FCSTD DOCUMENT  (FreeCAD 1.0R39285 (Git))
Label: folding_chair_02
License: CERN Open Hardware Licence permissive
LicenseURL: https://cern-ohl.web.cern.ch/
objects: Part::Feature×9, Sketcher::SketchObject×3, PartDesign::Body×2, Image::ImagePlane×1, PartDesign::SubShapeBinder×1
note: 18 computed .brp shape members not serialized (recipe doc carries the construction recipe); baked Part::Feature solids carry a one-line shape summary decoded from their .brp

FEATURE [Image::ImagePlane] flat_folding_chair_04
  Placement = pos=(40,-70,0) rot=(0,0,1;0rad)
  XSize = 80.0169
  YSize = 119.179
FEATURE [Part::Feature] path4
  shape: bbox 82.94 x 138.4 x 2e-07 mm, 0 faces, 0 solids (baked)
FEATURE [Part::Feature] path005
  shape: bbox 70.38 x 121.7 x 2e-07 mm, 0 faces, 0 solids (baked)
FEATURE [Part::Feature] path006
  shape: bbox 67.79 x 116.9 x 2e-07 mm, 0 faces, 0 solids (baked)
FEATURE [Part::Feature] path007
  shape: bbox 15.73 x 19.43 x 2e-07 mm, 0 faces, 0 solids (baked)
FEATURE [Part::Feature] path008
  shape: bbox 52.24 x 59.71 x 2e-07 mm, 0 faces, 0 solids (baked)
FEATURE [Part::Feature] path009
  shape: bbox 2.06 x 3.665 x 2e-07 mm, 0 faces, 0 solids (baked)
FEATURE [Part::Feature] path010
  shape: bbox 1.824 x 3.568 x 2e-07 mm, 0 faces, 0 solids (baked)
FEATURE [Part::Feature] path011
  shape: bbox 4.443 x 14.85 x 2e-07 mm, 0 faces, 0 solids (baked)
FEATURE [Part::Feature] path012
  shape: bbox 4.616 x 15.29 x 2e-07 mm, 0 faces, 0 solids (baked)
FEATURE [Sketcher::SketchObject] Sketch
  ArcFitTolerance = 1e-06
  AttachmentSupport = -> [XY_Plane]
  FullyConstrained = true
  MakeInternals = false
  MapMode = 5
  sketch-geometry (37):
    g0: LineSegment StartX=0 StartY=0 StartZ=0 EndX=0 EndY=-138.5 EndZ=0
    g1: LineSegment StartX=0 StartY=-138.5 StartZ=0 EndX=83 EndY=-138.5 EndZ=0
    g2: LineSegment StartX=83 StartY=-138.5 StartZ=0 EndX=83 EndY=0 EndZ=0
    g3: LineSegment StartX=83 StartY=0 StartZ=0 EndX=0 EndY=0 EndZ=0
    g4: LineSegment StartX=21.5 StartY=-68.75 StartZ=0 EndX=21.5 EndY=-128.75 EndZ=0
    g5: LineSegment StartX=21.5 StartY=-128.75 StartZ=0 EndX=61.5 EndY=-128.75 EndZ=0
    g6: LineSegment StartX=61.5 StartY=-128.75 StartZ=0 EndX=61.5 EndY=-68.75 EndZ=0
    g7: LineSegment StartX=61.5 StartY=-68.75 StartZ=0 EndX=21.5 EndY=-68.75 EndZ=0
    g8: LineSegment StartX=32.75 StartY=-63.75 StartZ=0 EndX=32.75 EndY=-68.75 EndZ=0
    g9: LineSegment StartX=32.75 StartY=-68.75 StartZ=0 EndX=50.25 EndY=-68.75 EndZ=0
    g10: LineSegment StartX=50.25 StartY=-68.75 StartZ=0 EndX=50.25 EndY=-63.75 EndZ=0
    g11: LineSegment StartX=50.25 StartY=-63.75 StartZ=0 EndX=32.75 EndY=-63.75 EndZ=0
    g12: LineSegment StartX=15.5 StartY=-10.75 StartZ=0 EndX=15.5 EndY=-48.75 EndZ=0
    g13: LineSegment StartX=15.5 StartY=-48.75 StartZ=0 EndX=67.5 EndY=-48.75 EndZ=0
    g14: LineSegment StartX=67.5 StartY=-48.75 StartZ=0 EndX=67.5 EndY=-10.75 EndZ=0
    g15: LineSegment StartX=67.5 StartY=-10.75 StartZ=0 EndX=15.5 EndY=-10.75 EndZ=0
    g16: LineSegment StartX=7.8 StartY=-10.75 StartZ=0 EndX=7.8 EndY=-50.25 EndZ=0
    g17: LineSegment StartX=7.8 StartY=-50.25 StartZ=0 EndX=14 EndY=-50.25 EndZ=0
    g18: LineSegment StartX=14 StartY=-50.25 StartZ=0 EndX=14 EndY=-10.75 EndZ=0
    g19: LineSegment StartX=14 StartY=-10.75 StartZ=0 EndX=7.8 EndY=-10.75 EndZ=0
    g20: LineSegment StartX=69 StartY=-10.75 StartZ=0 EndX=69 EndY=-50.25 EndZ=0
    g21: LineSegment StartX=69 StartY=-50.25 StartZ=0 EndX=75.2 EndY=-50.25 EndZ=0
    g22: LineSegment StartX=75.2 StartY=-50.25 StartZ=0 EndX=75.2 EndY=-10.75 EndZ=0
    g23: LineSegment StartX=75.2 StartY=-10.75 StartZ=0 EndX=69 EndY=-10.75 EndZ=0
    g24: LineSegment StartX=14 StartY=-135.25 StartZ=0 EndX=14 EndY=-138.5 EndZ=0
    g25: LineSegment StartX=14 StartY=-138.5 StartZ=0 EndX=69 EndY=-138.5 EndZ=0
    g26: LineSegment StartX=69 StartY=-138.5 StartZ=0 EndX=69 EndY=-135.25 EndZ=0
    g27: LineSegment StartX=69 StartY=-135.25 StartZ=0 EndX=14 EndY=-135.25 EndZ=0
    g28: LineSegment [constr] StartX=41.5 StartY=-138.5 StartZ=0 EndX=41.5 EndY=-135.25 EndZ=0
    g29: LineSegment [constr] StartX=41.5 StartY=-135.25 StartZ=0 EndX=41.5 EndY=-128.75 EndZ=0
    g30: LineSegment [constr] StartX=41.5 StartY=-128.75 StartZ=0 EndX=41.5 EndY=-94.75 EndZ=0
    g31: LineSegment [constr] StartX=41.5 StartY=-94.75 StartZ=0 EndX=41.5 EndY=-68.75 EndZ=0
    g32: LineSegment [constr] StartX=41.5 StartY=-68.75 StartZ=0 EndX=41.5 EndY=-63.75 EndZ=0
    g33: LineSegment [constr] StartX=41.5 StartY=-63.75 StartZ=0 EndX=41.5 EndY=-48.75 EndZ=0
    g34: LineSegment [constr] StartX=41.5 StartY=-48.75 StartZ=0 EndX=41.5 EndY=-10.75 EndZ=0
    g35: LineSegment [constr] StartX=41.5 StartY=-10.75 StartZ=0 EndX=41.5 EndY=0 EndZ=0
    g36: Circle [constr] CenterX=15.5 CenterY=-48.75 CenterZ=0 NormalX=0 NormalY=0 NormalZ=1 AngleXU=0 Radius=1.5
  constraints (102):
    c: Coincident(g0,g1)
    c: Coincident(g1,g2)
    c: Coincident(g2,g3)
    c: Coincident(g3,g0)
    c: Vertical(g0)
    c: Vertical(g2)
    c: Horizontal(g1)
    c: Horizontal(g3)
    c: Coincident(g0,g-1)
    c: DistanceX(g3,g3) = 83
    c: DistanceY(g0,g0) = 138.5
    c: Coincident(g4,g5)
    c: Coincident(g5,g6)
    c: Coincident(g6,g7)
    c: Coincident(g7,g4)
    c: Vertical(g4)
    c: Vertical(g6)
    c: Horizontal(g5)
    c: Horizontal(g7)
    c: Coincident(g8,g9)
    c: Coincident(g9,g10)
    c: Coincident(g10,g11)
    c: Coincident(g11,g8)
    c: Vertical(g8)
    c: Vertical(g10)
    c: Horizontal(g9)
    c: Horizontal(g11)
    c: Coincident(g12,g13)
    c: Coincident(g13,g14)
    c: Coincident(g14,g15)
    c: Coincident(g15,g12)
    c: Vertical(g12)
    c: Vertical(g14)
    c: Horizontal(g13)
    c: Horizontal(g15)
    c: Coincident(g16,g17)
    c: Coincident(g17,g18)
    c: Coincident(g18,g19)
    c: Coincident(g19,g16)
    c: Vertical(g16)
    c: Vertical(g18)
    c: Horizontal(g17)
    c: Horizontal(g19)
    c: Coincident(g20,g21)
    c: Coincident(g21,g22)
    c: Coincident(g22,g23)
    c: Coincident(g23,g20)
    c: Vertical(g20)
    c: Vertical(g22)
    c: Horizontal(g21)
    c: Horizontal(g23)
    c: Coincident(g24,g25)
    c: Coincident(g25,g26)
    c: Coincident(g26,g27)
    c: Coincident(g27,g24)
    c: Vertical(g24)
    c: Vertical(g26)
    c: Horizontal(g25)
    c: Horizontal(g27)
    c: Symmetric(g1,g1,g28)
    c: Coincident(g29,g28)
    c: Coincident(g30,g29)
    c: Vertical(g30)
    c: Coincident(g31,g30)
    c: Symmetric(g7,g7,g31)
    c: Coincident(g32,g31)
    c: Symmetric(g11,g11,g32)
    c: Coincident(g33,g32)
    c: Symmetric(g13,g13,g33)
    c: Vertical(g33)
    c: Coincident(g34,g33)
    c: Symmetric(g15,g15,g34)
    c: Coincident(g35,g34)
    c: Symmetric(g3,g3,g35)
    c: Vertical(g35)
    c: Vertical(g28)
    c: Vertical(g29)
    c: PointOnObject(g28,g27)
    c: PointOnObject(g29,g5)
    c: Vertical(g32)
    c: Symmetric(g24,g25,g28)
    c: Distance(g24,g24) = 3.25
    c: DistanceX(g27,g27) = 55
    c: DistanceY(g29,g29) = 6.5
    c: DistanceX(g5,g5) = 40
    c: DistanceY(g4,g4) = 60
    c: PointOnObject(g31,g9)
    c: DistanceY(g8,g8) = 5
    c: DistanceX(g11,g11) = 17.5
    c: DistanceY(g33,g33) = 15
    c: DistanceX(g13,g13) = 52
    c: DistanceY(g12,g12) = 38
    c: Equal(g19,g23)
    c: Equal(g18,g20)
    c: Symmetric(g18,g20,g35)
    c: Horizontal(g18,g12)
    c: DistanceX(g19,g19) = 6.2
    c: Distance(g18,g12) = 1.5
    c: DistanceY(g30,g30) = 34
    c: Coincident(g36,g12)
    c: Tangent(g36,g18)
    c: Tangent(g17,g36)
FEATURE [PartDesign::Body] Body
  AllowCompound = false
  Group = -> [Sketch]
  Origin = -> Origin
FEATURE [Sketcher::SketchObject] Sketch001
  ArcFitTolerance = 1e-06
  FullyConstrained = false
  MakeInternals = false
  sketch-geometry (161):
    g0: BSplineCurve PolesCount=2 KnotsCount=2 Degree=1 IsPeriodic=0
    g1: BSplineCurve PolesCount=2 KnotsCount=2 Degree=1 IsPeriodic=0
    g2: BSplineCurve PolesCount=2 KnotsCount=2 Degree=1 IsPeriodic=0
    g3: BSplineCurve PolesCount=2 KnotsCount=2 Degree=1 IsPeriodic=0
    g4: BSplineCurve PolesCount=2 KnotsCount=2 Degree=1 IsPeriodic=0
    g5: BSplineCurve PolesCount=2 KnotsCount=2 Degree=1 IsPeriodic=0
    g6: BSplineCurve PolesCount=4 KnotsCount=2 Degree=3 IsPeriodic=0
    g7: BSplineCurve PolesCount=4 KnotsCount=2 Degree=3 IsPeriodic=0
    g8: BSplineCurve PolesCount=2 KnotsCount=2 Degree=1 IsPeriodic=0
    g9: BSplineCurve PolesCount=2 KnotsCount=2 Degree=1 IsPeriodic=0
    g10: BSplineCurve PolesCount=2 KnotsCount=2 Degree=1 IsPeriodic=0
    g11: BSplineCurve PolesCount=2 KnotsCount=2 Degree=1 IsPeriodic=0
    g12: BSplineCurve PolesCount=4 KnotsCount=2 Degree=3 IsPeriodic=0
    g13: BSplineCurve PolesCount=4 KnotsCount=2 Degree=3 IsPeriodic=0
    g14: BSplineCurve PolesCount=4 KnotsCount=2 Degree=3 IsPeriodic=0
    g15: BSplineCurve PolesCount=4 KnotsCount=2 Degree=3 IsPeriodic=0
    g16: BSplineCurve PolesCount=4 KnotsCount=2 Degree=3 IsPeriodic=0
    g17: BSplineCurve PolesCount=4 KnotsCount=2 Degree=3 IsPeriodic=0
    g18: BSplineCurve PolesCount=4 KnotsCount=2 Degree=3 IsPeriodic=0
    g19: BSplineCurve PolesCount=4 KnotsCount=2 Degree=3 IsPeriodic=0
    g20: BSplineCurve PolesCount=4 KnotsCount=2 Degree=3 IsPeriodic=0
    g21: BSplineCurve PolesCount=4 KnotsCount=2 Degree=3 IsPeriodic=0
    g22: BSplineCurve PolesCount=4 KnotsCount=2 Degree=3 IsPeriodic=0
    g23: BSplineCurve PolesCount=4 KnotsCount=2 Degree=3 IsPeriodic=0
    g24: BSplineCurve PolesCount=4 KnotsCount=2 Degree=3 IsPeriodic=0
    g25: BSplineCurve PolesCount=4 KnotsCount=2 Degree=3 IsPeriodic=0
    g26: BSplineCurve PolesCount=2 KnotsCount=2 Degree=1 IsPeriodic=0
    g27: BSplineCurve PolesCount=2 KnotsCount=2 Degree=1 IsPeriodic=0
    g28: BSplineCurve PolesCount=4 KnotsCount=2 Degree=3 IsPeriodic=0
    g29: BSplineCurve PolesCount=4 KnotsCount=2 Degree=3 IsPeriodic=0
    g30: BSplineCurve PolesCount=2 KnotsCount=2 Degree=1 IsPeriodic=0
    g31: BSplineCurve PolesCount=2 KnotsCount=2 Degree=1 IsPeriodic=0
    g32: BSplineCurve PolesCount=4 KnotsCount=2 Degree=3 IsPeriodic=0
    g33: BSplineCurve PolesCount=4 KnotsCount=2 Degree=3 IsPeriodic=0
    g34: BSplineCurve PolesCount=2 KnotsCount=2 Degree=1 IsPeriodic=0
    g35: BSplineCurve PolesCount=2 KnotsCount=2 Degree=1 IsPeriodic=0
    g36: BSplineCurve PolesCount=2 KnotsCount=2 Degree=1 IsPeriodic=0
    g37: BSplineCurve PolesCount=2 KnotsCount=2 Degree=1 IsPeriodic=0
    g38: BSplineCurve PolesCount=4 KnotsCount=2 Degree=3 IsPeriodic=0
    g39: BSplineCurve PolesCount=4 KnotsCount=2 Degree=3 IsPeriodic=0
    g40: BSplineCurve PolesCount=4 KnotsCount=2 Degree=3 IsPeriodic=0
    g41: BSplineCurve PolesCount=4 KnotsCount=2 Degree=3 IsPeriodic=0
    g42: BSplineCurve PolesCount=4 KnotsCount=2 Degree=3 IsPeriodic=0
    g43: BSplineCurve PolesCount=4 KnotsCount=2 Degree=3 IsPeriodic=0
    g44: BSplineCurve PolesCount=4 KnotsCount=2 Degree=3 IsPeriodic=0
    g45: BSplineCurve PolesCount=4 KnotsCount=2 Degree=3 IsPeriodic=0
    g46: BSplineCurve PolesCount=4 KnotsCount=2 Degree=3 IsPeriodic=0
    g47: BSplineCurve PolesCount=2 KnotsCount=2 Degree=1 IsPeriodic=0
    g48: BSplineCurve PolesCount=2 KnotsCount=2 Degree=1 IsPeriodic=0
    g49: BSplineCurve PolesCount=4 KnotsCount=2 Degree=3 IsPeriodic=0
    g50: BSplineCurve PolesCount=4 KnotsCount=2 Degree=3 IsPeriodic=0
    g51: BSplineCurve PolesCount=2 KnotsCount=2 Degree=1 IsPeriodic=0
    g52: BSplineCurve PolesCount=2 KnotsCount=2 Degree=1 IsPeriodic=0
    g53: BSplineCurve PolesCount=4 KnotsCount=2 Degree=3 IsPeriodic=0
    g54: BSplineCurve PolesCount=4 KnotsCount=2 Degree=3 IsPeriodic=0
    g55: BSplineCurve PolesCount=4 KnotsCount=2 Degree=3 IsPeriodic=0
    g56: BSplineCurve PolesCount=2 KnotsCount=2 Degree=1 IsPeriodic=0
    g57: BSplineCurve PolesCount=2 KnotsCount=2 Degree=1 IsPeriodic=0
    g58: BSplineCurve PolesCount=4 KnotsCount=2 Degree=3 IsPeriodic=0
    g59: BSplineCurve PolesCount=4 KnotsCount=2 Degree=3 IsPeriodic=0
    g60: BSplineCurve PolesCount=4 KnotsCount=2 Degree=3 IsPeriodic=0
    g61: BSplineCurve PolesCount=2 KnotsCount=2 Degree=1 IsPeriodic=0
    g62: BSplineCurve PolesCount=2 KnotsCount=2 Degree=1 IsPeriodic=0
    g63: BSplineCurve PolesCount=2 KnotsCount=2 Degree=1 IsPeriodic=0
    g64: BSplineCurve PolesCount=2 KnotsCount=2 Degree=1 IsPeriodic=0
    g65: BSplineCurve PolesCount=2 KnotsCount=2 Degree=1 IsPeriodic=0
    g66: BSplineCurve PolesCount=4 KnotsCount=2 Degree=3 IsPeriodic=0
    g67: BSplineCurve PolesCount=4 KnotsCount=2 Degree=3 IsPeriodic=0
    g68: BSplineCurve PolesCount=4 KnotsCount=2 Degree=3 IsPeriodic=0
    g69: BSplineCurve PolesCount=2 KnotsCount=2 Degree=1 IsPeriodic=0
    g70: BSplineCurve PolesCount=2 KnotsCount=2 Degree=1 IsPeriodic=0
    g71: BSplineCurve PolesCount=4 KnotsCount=2 Degree=3 IsPeriodic=0
    g72: BSplineCurve PolesCount=4 KnotsCount=2 Degree=3 IsPeriodic=0
    g73: BSplineCurve PolesCount=4 KnotsCount=2 Degree=3 IsPeriodic=0
    g74: BSplineCurve PolesCount=4 KnotsCount=2 Degree=3 IsPeriodic=0
    g75: BSplineCurve PolesCount=2 KnotsCount=2 Degree=1 IsPeriodic=0
    g76: BSplineCurve PolesCount=2 KnotsCount=2 Degree=1 IsPeriodic=0
    g77: BSplineCurve PolesCount=2 KnotsCount=2 Degree=1 IsPeriodic=0
    g78: BSplineCurve PolesCount=2 KnotsCount=2 Degree=1 IsPeriodic=0
    g79: BSplineCurve PolesCount=4 KnotsCount=2 Degree=3 IsPeriodic=0
    g80: BSplineCurve PolesCount=4 KnotsCount=2 Degree=3 IsPeriodic=0
    g81: BSplineCurve PolesCount=4 KnotsCount=2 Degree=3 IsPeriodic=0
    g82: BSplineCurve PolesCount=2 KnotsCount=2 Degree=1 IsPeriodic=0
    g83: BSplineCurve PolesCount=2 KnotsCount=2 Degree=1 IsPeriodic=0
    g84: BSplineCurve PolesCount=4 KnotsCount=2 Degree=3 IsPeriodic=0
    g85: BSplineCurve PolesCount=4 KnotsCount=2 Degree=3 IsPeriodic=0
    g86: BSplineCurve PolesCount=2 KnotsCount=2 Degree=1 IsPeriodic=0
    g87: BSplineCurve PolesCount=2 KnotsCount=2 Degree=1 IsPeriodic=0
    g88: BSplineCurve PolesCount=4 KnotsCount=2 Degree=3 IsPeriodic=0
    g89: BSplineCurve PolesCount=4 KnotsCount=2 Degree=3 IsPeriodic=0
    g90: BSplineCurve PolesCount=2 KnotsCount=2 Degree=1 IsPeriodic=0
    g91: BSplineCurve PolesCount=2 KnotsCount=2 Degree=1 IsPeriodic=0
    g92: BSplineCurve PolesCount=4 KnotsCount=2 Degree=3 IsPeriodic=0
    g93: BSplineCurve PolesCount=4 KnotsCount=2 Degree=3 IsPeriodic=0
    g94: BSplineCurve PolesCount=4 KnotsCount=2 Degree=3 IsPeriodic=0
    g95: BSplineCurve PolesCount=4 KnotsCount=2 Degree=3 IsPeriodic=0
    g96: BSplineCurve PolesCount=4 KnotsCount=2 Degree=3 IsPeriodic=0
    g97: BSplineCurve PolesCount=2 KnotsCount=2 Degree=1 IsPeriodic=0
    g98: BSplineCurve PolesCount=2 KnotsCount=2 Degree=1 IsPeriodic=0
    g99: BSplineCurve PolesCount=4 KnotsCount=2 Degree=3 IsPeriodic=0
    g100: BSplineCurve PolesCount=4 KnotsCount=2 Degree=3 IsPeriodic=0
    g101: BSplineCurve PolesCount=4 KnotsCount=2 Degree=3 IsPeriodic=0
    g102: BSplineCurve PolesCount=4 KnotsCount=2 Degree=3 IsPeriodic=0
    g103: BSplineCurve PolesCount=2 KnotsCount=2 Degree=1 IsPeriodic=0
    g104: BSplineCurve PolesCount=2 KnotsCount=2 Degree=1 IsPeriodic=0
    g105: BSplineCurve PolesCount=4 KnotsCount=2 Degree=3 IsPeriodic=0
    g106: BSplineCurve PolesCount=4 KnotsCount=2 Degree=3 IsPeriodic=0
    g107: BSplineCurve PolesCount=4 KnotsCount=2 Degree=3 IsPeriodic=0
    g108: BSplineCurve PolesCount=4 KnotsCount=2 Degree=3 IsPeriodic=0
    g109: BSplineCurve PolesCount=2 KnotsCount=2 Degree=1 IsPeriodic=0
    g110: BSplineCurve PolesCount=4 KnotsCount=2 Degree=3 IsPeriodic=0
    g111: BSplineCurve PolesCount=2 KnotsCount=2 Degree=1 IsPeriodic=0
    g112: BSplineCurve PolesCount=2 KnotsCount=2 Degree=1 IsPeriodic=0
    g113: BSplineCurve PolesCount=4 KnotsCount=2 Degree=3 IsPeriodic=0
    g114: BSplineCurve PolesCount=4 KnotsCount=2 Degree=3 IsPeriodic=0
    g115: BSplineCurve PolesCount=4 KnotsCount=2 Degree=3 IsPeriodic=0
    g116: BSplineCurve PolesCount=4 KnotsCount=2 Degree=3 IsPeriodic=0
    g117: BSplineCurve PolesCount=4 KnotsCount=2 Degree=3 IsPeriodic=0
    g118: BSplineCurve PolesCount=4 KnotsCount=2 Degree=3 IsPeriodic=0
    g119: BSplineCurve PolesCount=4 KnotsCount=2 Degree=3 IsPeriodic=0
    g120: BSplineCurve PolesCount=4 KnotsCount=2 Degree=3 IsPeriodic=0
    g121: BSplineCurve PolesCount=4 KnotsCount=2 Degree=3 IsPeriodic=0
    g122: BSplineCurve PolesCount=4 KnotsCount=2 Degree=3 IsPeriodic=0
    g123: BSplineCurve PolesCount=2 KnotsCount=2 Degree=1 IsPeriodic=0
    g124: BSplineCurve PolesCount=4 KnotsCount=2 Degree=3 IsPeriodic=0
    g125: BSplineCurve PolesCount=4 KnotsCount=2 Degree=3 IsPeriodic=0
    g126: BSplineCurve PolesCount=4 KnotsCount=2 Degree=3 IsPeriodic=0
    g127: BSplineCurve PolesCount=4 KnotsCount=2 Degree=3 IsPeriodic=0
    g128: BSplineCurve PolesCount=2 KnotsCount=2 Degree=1 IsPeriodic=0
    g129: BSplineCurve PolesCount=2 KnotsCount=2 Degree=1 IsPeriodic=0
    g130: BSplineCurve PolesCount=4 KnotsCount=2 Degree=3 IsPeriodic=0
    g131: BSplineCurve PolesCount=4 KnotsCount=2 Degree=3 IsPeriodic=0
    g132: BSplineCurve PolesCount=4 KnotsCount=2 Degree=3 IsPeriodic=0
    g133: BSplineCurve PolesCount=2 KnotsCount=2 Degree=1 IsPeriodic=0
    g134: BSplineCurve PolesCount=2 KnotsCount=2 Degree=1 IsPeriodic=0
    g135: BSplineCurve PolesCount=4 KnotsCount=2 Degree=3 IsPeriodic=0
    g136: BSplineCurve PolesCount=4 KnotsCount=2 Degree=3 IsPeriodic=0
    g137: BSplineCurve PolesCount=4 KnotsCount=2 Degree=3 IsPeriodic=0
    g138: BSplineCurve PolesCount=4 KnotsCount=2 Degree=3 IsPeriodic=0
    g139: BSplineCurve PolesCount=4 KnotsCount=2 Degree=3 IsPeriodic=0
    g140: BSplineCurve PolesCount=4 KnotsCount=2 Degree=3 IsPeriodic=0
    g141: BSplineCurve PolesCount=4 KnotsCount=2 Degree=3 IsPeriodic=0
    g142: BSplineCurve PolesCount=4 KnotsCount=2 Degree=3 IsPeriodic=0
    g143: BSplineCurve PolesCount=4 KnotsCount=2 Degree=3 IsPeriodic=0
    g144: BSplineCurve PolesCount=4 KnotsCount=2 Degree=3 IsPeriodic=0
    g145: BSplineCurve PolesCount=4 KnotsCount=2 Degree=3 IsPeriodic=0
    g146: BSplineCurve PolesCount=4 KnotsCount=2 Degree=3 IsPeriodic=0
    g147: BSplineCurve PolesCount=4 KnotsCount=2 Degree=3 IsPeriodic=0
    g148: BSplineCurve PolesCount=4 KnotsCount=2 Degree=3 IsPeriodic=0
    g149: BSplineCurve PolesCount=4 KnotsCount=2 Degree=3 IsPeriodic=0
    g150: BSplineCurve PolesCount=4 KnotsCount=2 Degree=3 IsPeriodic=0
    g151: BSplineCurve PolesCount=4 KnotsCount=2 Degree=3 IsPeriodic=0
    g152: BSplineCurve PolesCount=4 KnotsCount=2 Degree=3 IsPeriodic=0
    g153: BSplineCurve PolesCount=4 KnotsCount=2 Degree=3 IsPeriodic=0
    g154: BSplineCurve PolesCount=4 KnotsCount=2 Degree=3 IsPeriodic=0
    g155: BSplineCurve PolesCount=2 KnotsCount=2 Degree=1 IsPeriodic=0
    g156: BSplineCurve PolesCount=4 KnotsCount=2 Degree=3 IsPeriodic=0
    g157: BSplineCurve PolesCount=4 KnotsCount=2 Degree=3 IsPeriodic=0
    g158: BSplineCurve PolesCount=4 KnotsCount=2 Degree=3 IsPeriodic=0
    g159: BSplineCurve PolesCount=4 KnotsCount=2 Degree=3 IsPeriodic=0
    g160: BSplineCurve PolesCount=4 KnotsCount=2 Degree=3 IsPeriodic=0
  constraints (161):
    c: Coincident(g0,g1)
    c: Coincident(g1,g2)
    c: Coincident(g2,g3)
    c: Coincident(g3,g4)
    c: Coincident(g4,g5)
    c: Coincident(g5,g6)
    c: Coincident(g6,g7)
    c: Coincident(g7,g8)
    c: Coincident(g8,g9)
    c: Coincident(g9,g10)
    c: Coincident(g10,g11)
    c: Coincident(g11,g12)
    c: Coincident(g12,g13)
    c: Coincident(g13,g14)
    c: Coincident(g14,g15)
    c: Coincident(g15,g16)
    c: Coincident(g16,g17)
    c: Coincident(g17,g18)
    c: Coincident(g18,g19)
    c: Coincident(g19,g20)
    c: Coincident(g20,g21)
    c: Coincident(g21,g22)
    c: Coincident(g22,g23)
    c: Coincident(g23,g24)
    c: Coincident(g24,g25)
    c: Coincident(g25,g26)
    c: Coincident(g26,g27)
    c: Coincident(g27,g0)
    c: Coincident(g28,g29)
    c: Coincident(g29,g30)
    c: Coincident(g30,g31)
    c: Coincident(g31,g32)
    c: Coincident(g32,g33)
    c: Coincident(g33,g34)
    c: Coincident(g34,g35)
    c: Coincident(g35,g36)
    c: Coincident(g36,g37)
    c: Coincident(g37,g38)
    c: Coincident(g38,g39)
    c: Coincident(g39,g40)
    c: Coincident(g40,g41)
    c: Coincident(g41,g42)
    c: Coincident(g42,g43)
    c: Coincident(g43,g44)
    c: Coincident(g44,g45)
    c: Coincident(g45,g46)
    c: Coincident(g46,g47)
    c: Coincident(g47,g48)
    c: Coincident(g48,g49)
    c: Coincident(g49,g50)
    c: Coincident(g50,g51)
    c: Coincident(g51,g52)
    c: Coincident(g52,g53)
    c: Coincident(g53,g54)
    c: Coincident(g54,g55)
    c: Coincident(g55,g56)
    c: Coincident(g56,g57)
    c: Coincident(g57,g58)
    c: Coincident(g58,g59)
    c: Coincident(g59,g60)
    c: Coincident(g60,g61)
    c: Coincident(g61,g28)
    c: Coincident(g62,g63)
    c: Coincident(g63,g64)
    c: Coincident(g64,g65)
    c: Coincident(g65,g66)
    c: Coincident(g66,g67)
    c: Coincident(g67,g68)
    c: Coincident(g68,g69)
    c: Coincident(g69,g70)
    c: Coincident(g70,g71)
    c: Coincident(g71,g72)
    c: Coincident(g72,g73)
    c: Coincident(g73,g74)
    c: Coincident(g74,g75)
    c: Coincident(g75,g76)
    c: Coincident(g76,g77)
    c: Coincident(g77,g78)
    c: Coincident(g78,g79)
    c: Coincident(g79,g80)
    c: Coincident(g80,g81)
    c: Coincident(g81,g82)
    c: Coincident(g82,g83)
    c: Coincident(g83,g84)
    c: Coincident(g84,g85)
    c: Coincident(g85,g86)
    c: Coincident(g86,g87)
    c: Coincident(g87,g88)
    c: Coincident(g88,g89)
    c: Coincident(g89,g90)
    c: Coincident(g90,g91)
    c: Coincident(g91,g92)
    c: Coincident(g92,g93)
    c: Coincident(g93,g94)
    c: Coincident(g94,g95)
    c: Coincident(g95,g96)
    c: Coincident(g96,g97)
    c: Coincident(g97,g98)
    c: Coincident(g98,g99)
    c: Coincident(g99,g100)
    c: Coincident(g100,g101)
    c: Coincident(g101,g102)
    c: Coincident(g102,g103)
    c: Coincident(g103,g104)
    c: Coincident(g104,g105)
    c: Coincident(g105,g106)
    c: Coincident(g106,g107)
    c: Coincident(g107,g108)
    c: Coincident(g108,g109)
    c: Coincident(g109,g62)
    c: Coincident(g110,g111)
    c: Coincident(g111,g112)
    c: Coincident(g112,g113)
    c: Coincident(g113,g114)
    c: Coincident(g114,g115)
    c: Coincident(g115,g116)
    c: Coincident(g116,g117)
    c: Coincident(g117,g118)
    c: Coincident(g118,g119)
    c: Coincident(g119,g120)
    c: Coincident(g120,g121)
    c: Coincident(g121,g122)
    c: Coincident(g122,g123)
    c: Coincident(g123,g110)
    c: Coincident(g124,g125)
    c: Coincident(g125,g126)
    c: Coincident(g126,g127)
    c: Coincident(g127,g128)
    c: Coincident(g128,g129)
    c: Coincident(g129,g130)
    c: Coincident(g130,g131)
    c: Coincident(g131,g132)
    c: Coincident(g132,g133)
    c: Coincident(g133,g134)
    c: Coincident(g134,g135)
    c: Coincident(g135,g136)
    c: Coincident(g136,g137)
    c: Coincident(g137,g138)
    c: Coincident(g138,g139)
    c: Coincident(g139,g124)
    c: Coincident(g140,g141)
    c: Coincident(g141,g142)
    c: Coincident(g142,g140)
    c: Coincident(g143,g144)
    c: Coincident(g144,g145)
    c: Coincident(g145,g146)
    c: Coincident(g146,g143)
    c: Coincident(g147,g148)
    c: Coincident(g148,g149)
    c: Coincident(g149,g150)
    c: Coincident(g150,g151)
    c: Coincident(g151,g152)
    c: Coincident(g152,g153)
    c: Coincident(g153,g154)
    c: Coincident(g154,g155)
    c: Coincident(g155,g147)
    c: Coincident(g156,g157)
    c: Coincident(g157,g158)
    c: Coincident(g158,g159)
    c: Coincident(g159,g160)
    c: Coincident(g160,g156)
FEATURE [PartDesign::SubShapeBinder] Binder
  BindCopyOnChange = 0
  BindMode = 0
  ClaimChildren = false
  Context = -> Body001 [Binder.]
  Fuse = false
  MakeFace = true
  OffsetFill = false
  OffsetIntersection = false
  OffsetJoinType = 0
  OffsetOpenResult = false
  PartialLoad = false
  Refine = true
  Relative = true
  Support = -> [Body[Sketch.]]
  _Version = 2
FEATURE [Sketcher::SketchObject] Sketch002
  ArcFitTolerance = 1e-06
  AttachmentSupport = -> [XY_Plane001]
  ExternalGeometry = -> [Binder]
  FullyConstrained = true
  MakeInternals = false
  MapMode = 5
  sketch-geometry (23):
    g0: LineSegment [constr] StartX=0 StartY=-138.5 StartZ=0 EndX=83 EndY=-138.5 EndZ=0
    g1: ArcOfCircle CenterX=7.25 CenterY=-11.0878 CenterZ=0 NormalX=0 NormalY=0 NormalZ=1 AngleXU=0 Radius=7.25 StartAngle=1.79397 EndAngle=3.14159
    g2: ArcOfCircle CenterX=75.75 CenterY=-11.0878 CenterZ=0 NormalX=0 NormalY=0 NormalZ=1 AngleXU=0 Radius=7.25 StartAngle=3.01745e-06 EndAngle=1.34762
    g3: LineSegment [constr] StartX=41.5 StartY=0 StartZ=0 EndX=41.5 EndY=-138.5 EndZ=0
    g4: ArcOfCircle CenterX=41.5 CenterY=-162 CenterZ=0 NormalX=0 NormalY=0 NormalZ=1 AngleXU=0 Radius=162 StartAngle=1.34762 EndAngle=1.79397
    g5: LineSegment StartX=0 StartY=-11.0878 StartZ=0 EndX=0 EndY=-131.25 EndZ=0
    g6: LineSegment StartX=83 StartY=-11.0878 StartZ=0 EndX=83 EndY=-131.25 EndZ=0
    g7: ArcOfCircle CenterX=7.25 CenterY=-131.25 CenterZ=0 NormalX=0 NormalY=0 NormalZ=1 AngleXU=0 Radius=7.25 StartAngle=3.14159 EndAngle=4.71239
    g8: ArcOfCircle CenterX=75.75 CenterY=-131.25 CenterZ=0 NormalX=0 NormalY=0 NormalZ=1 AngleXU=0 Radius=7.25 StartAngle=4.71239 EndAngle=6.28319
    g9: LineSegment StartX=7.25 StartY=-138.5 StartZ=0 EndX=14 EndY=-138.5 EndZ=0
    g10: LineSegment StartX=75.75 StartY=-138.5 StartZ=0 EndX=69 EndY=-138.5 EndZ=0
    g11: LineSegment StartX=14 StartY=-138.5 StartZ=0 EndX=17.25 EndY=-135.25 EndZ=0
    g12: LineSegment StartX=17.25 StartY=-135.25 StartZ=0 EndX=65.75 EndY=-135.25 EndZ=0
    g13: LineSegment StartX=65.75 StartY=-135.25 StartZ=0 EndX=69 EndY=-138.5 EndZ=0
    g14: LineSegment StartX=4.8 StartY=-72.5 StartZ=0 EndX=4.8 EndY=-84.5 EndZ=0
    g15: ArcOfCircle CenterX=6 CenterY=-84.5 CenterZ=0 NormalX=0 NormalY=0 NormalZ=1 AngleXU=0 Radius=1.2 StartAngle=3.14159 EndAngle=5.69415
    g16: ArcOfCircle CenterX=-2.97998 CenterY=-78.5 CenterZ=0 NormalX=0 NormalY=0 NormalZ=1 AngleXU=0 Radius=12 StartAngle=5.69415 EndAngle=6.87222
    g17: ArcOfCircle CenterX=6 CenterY=-72.5 CenterZ=0 NormalX=0 NormalY=0 NormalZ=1 AngleXU=0 Radius=1.2 StartAngle=0.589031 EndAngle=3.14159
    g18: LineSegment [constr] StartX=4.8 StartY=-78.5 StartZ=0 EndX=0 EndY=-78.5 EndZ=0
    g19: LineSegment StartX=78.2 StartY=-72.5 StartZ=0 EndX=78.2 EndY=-84.5 EndZ=0
    g20: ArcOfCircle CenterX=77 CenterY=-84.5 CenterZ=0 NormalX=0 NormalY=0 NormalZ=1 AngleXU=0 Radius=1.2 StartAngle=3.73062 EndAngle=6.28319
    g21: ArcOfCircle CenterX=85.98 CenterY=-78.5 CenterZ=0 NormalX=0 NormalY=0 NormalZ=1 AngleXU=0 Radius=12 StartAngle=2.55256 EndAngle=3.73062
    g22: ArcOfCircle CenterX=77 CenterY=-72.5 CenterZ=0 NormalX=0 NormalY=0 NormalZ=1 AngleXU=0 Radius=1.2 StartAngle=0 EndAngle=2.55256
  constraints (53):
    c: Coincident(g0,g-3)
    c: Symmetric(g0,g0,g3)
    c: Symmetric(g1,g2,g3)
    c: Equal(g1,g2)
    c: Tangent(g4,g1) = -1.5708
    c: Tangent(g4,g2) = -1.5708
    c: Radius(g1) = 7.25
    c: Radius(g4) = 162
    c: Tangent(g5,g1) = -1.5708
    c: Coincident(g6,g2)
    c: Equal(g6,g5)
    c: Tangent(g7,g5) = -1.5708
    c: Tangent(g7,g0) = -1.5708
    c: Equal(g7,g1)
    c: Coincident(g8,g6)
    c: Equal(g8,g7)
    c: Tangent(g8,g0) = -1.5708
    c: Tangent(g9,g7) = -1.5708
    c: Coincident(g10,g8)
    c: Coincident(g10,g-3)
    c: Coincident(g9,g-4)
    c: Coincident(g9,g11)
    c: Coincident(g11,g12)
    c: Coincident(g12,g13)
    c: Coincident(g13,g10)
    c: Horizontal(g-4,g11)
    c: Symmetric(g12,g11,g3)
    c: Angle(g0,g11) = 0.785398
    c: Vertical(g14)
    c: Tangent(g14,g15) = -1.5708
    c: Tangent(g15,g16) = -1.5708
    c: Tangent(g16,g17) = -1.5708
    c: Tangent(g17,g14) = -1.5708
    c: Equal(g15,g17)
    c: DistanceY(g14,g14) = 12
    c: Radius(g17) = 1.2
    c: Radius(g16) = 12
    c: Distance(g17,g5) = 6
    c: Symmetric(g14,g14,g18)
    c: PointOnObject(g18,g5)
    c: Horizontal(g18)
    c: DistanceY(g0,g18) = 60
    c: Symmetric(g14,g19,g3)
    c: Symmetric(g14,g19,g3)
    c: Equal(g15,g20)
    c: Symmetric(g15,g20,g3)
    c: Symmetric(g15,g20,g3)
    c: Equal(g16,g21)
    c: Symmetric(g16,g21,g3)
    c: Symmetric(g16,g21,g3)
    c: Equal(g17,g22)
    c: Symmetric(g17,g22,g3)
    c: Symmetric(g17,g22,g3)
FEATURE [PartDesign::Body] Body001
  AllowCompound = false
  Group = -> [Sketch002,Binder]
  Origin = -> Origin001
